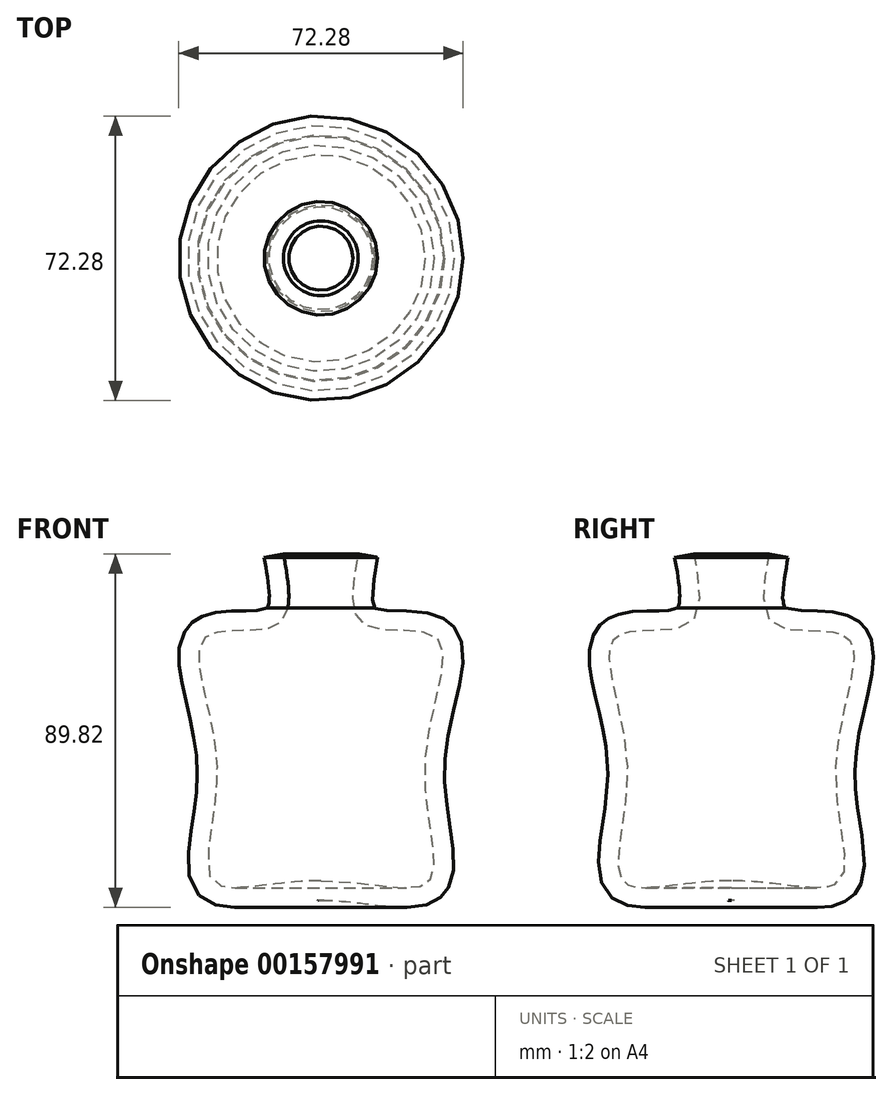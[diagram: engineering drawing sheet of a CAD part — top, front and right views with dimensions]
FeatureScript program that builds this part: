
annotation { "Feature Type Name" : "Feature", "Feature Type Description" : "" }
export const myFeature = defineFeature(function(context is Context, id is Id, definition is map)
    precondition{}
    {
        {
            var Q0;
            Q0=qCreatedBy(makeId("Front.planeOp"),FACE);
            var sketch = newSketch(context, id + "F0", { "sketchPlane" : qUnion([Q0])});
            skFitSpline(sketch, "E0", {"points": [v(0, 0) * mm, v(27.57, 0) * mm, v(26.48, 29.93) * mm, v(29.5, 61.75) * mm, v(11.1, 64.97) * mm, v(9.5, 83.03) * mm], "startDerivative": vector(183.77, -0.53) * mm, "endDerivative": vector(24.04, 135.45) * mm});
            skFitSpline(sketch, "E1.0", {"points": [v(-0.01, -5) * mm, v(1.75, -5) * mm, v(5.27, -5.17) * mm, v(10.39, -5.7) * mm, v(14.42, -6.21) * mm, v(17.49, -6.54) * mm, v(19.7, -6.72) * mm, v(21.87, -6.8) * mm, v(24, -6.7) * mm, v(25.78, -6.43) * mm, v(27.24, -6.01) * mm, v(28.35, -5.57) * mm, v(29.46, -4.96) * mm, v(30.34, -4.3) * mm, v(31, -3.67) * mm, v(31.46, -3.15) * mm, v(31.87, -2.6) * mm, v(32.35, -1.86) * mm, v(32.83, -0.9) * mm, v(33.37, 0.61) * mm, v(33.7, 2.46) * mm, v(33.8, 4.6) * mm, v(33.7, 6.75) * mm, v(33.5, 8.94) * mm, v(33.2, 11.2) * mm, v(32.84, 13.52) * mm, v(32.47, 15.9) * mm, v(32.12, 18.36) * mm, v(31.81, 20.85) * mm, v(31.57, 23.38) * mm, v(31.43, 25.9) * mm, v(31.4, 28.43) * mm, v(31.53, 30.92) * mm, v(31.81, 33.48) * mm, v(32.22, 36.09) * mm, v(32.72, 38.7) * mm, v(33.48, 42.2) * mm, v(34.3, 45.62) * mm, v(35.03, 48.93) * mm, v(35.52, 51.35) * mm, v(35.9, 53.71) * mm, v(36.11, 56.04) * mm, v(36.1, 58.37) * mm, v(35.8, 60.37) * mm, v(35.27, 62.02) * mm, v(34.68, 63.25) * mm, v(34, 64.24) * mm, v(33.37, 64.98) * mm, v(32.83, 65.5) * mm, v(32.26, 65.96) * mm, v(31.5, 66.5) * mm, v(30.51, 67.03) * mm, v(29.35, 67.5) * mm, v(27.84, 67.94) * mm, v(26.01, 68.27) * mm, v(23.88, 68.46) * mm, v(21.8, 68.54) * mm, v(19.81, 68.57) * mm, v(17.95, 68.62) * mm, v(16.3, 68.7) * mm, v(15.16, 68.85) * mm, v(14.46, 69) * mm, v(14.05, 69.1) * mm, v(13.83, 69.19) * mm, v(13.72, 69.24) * mm, v(13.68, 69.26) * mm, v(13.67, 69.27) * mm, v(13.66, 69.27) * mm, v(13.66, 69.27) * mm, v(13.65, 69.28) * mm, v(13.61, 69.34) * mm, v(13.54, 69.46) * mm, v(13.43, 69.74) * mm, v(13.27, 70.33) * mm, v(13.15, 71.4) * mm, v(13.14, 72.75) * mm, v(13.26, 74.87) * mm, v(13.68, 77.98) * mm, v(14.17, 80.75) * mm, v(14.42, 82.16) * mm]});
            skLineSegment(sketch, "E2", {"start": v(9.5, 83.03) * mm, "end": v(14.42, 82.16) * mm});
            skLineSegment(sketch, "E3", {"start": v(0, 0) * mm, "end": v(0, -5) * mm});
            skSolve(sketch);
        }
        {
            var Q0;
            Q0=makeQuery(id+"F0.imprint","IMPRINT",FACE,{"disambiguationData":[TD([[makeQuery(id+"F0.imprint","IMPRINT",EDGE,{"derivedFrom":sQuery(id+"F0.wireOp",EDGE,"E0")}),-1.0]])]});
            var Q1;
            Q1=sQuery(id+"F0.wireOp",EDGE,"E3");
            revolve(context, id + "F1", {"entities" : qUnion([Q0]), "axis" : qUnion([Q1]), "revolveType" : RevolveType.FULL});
        }
        {
            var Q0;
            Q0=qCreatedBy(makeId("Right.planeOp"),FACE);
            var sketch = newSketch(context, id + "F2", { "sketchPlane" : qUnion([Q0])});
            skFitSpline(sketch, "E4", {"points": [v(-32.27, 56.49) * mm, v(-49.92, 56.02) * mm, v(-40.53, 32.25) * mm, v(-29.8, 31.98) * mm], "startDerivative": vector(-63.25, 47.52) * mm, "endDerivative": vector(43.98, 18.52) * mm});
            skSolve(sketch);
        }
        {
            var Q0;
            Q0=sQuery(id+"F2.wireOp",VERTEX,"E4.0.internal");
            var Q1;
            Q1=sQuery(id+"F2.wireOp",EDGE,"E4");
            cPlane(context, id + "F3", {"entities" : qUnion([Q0, Q1]), "cplaneType" : CPlaneType.CURVE_POINT, "offset" : 25 * mm, "width" : 150 * mm, "height" : 150 * mm});
        }
    });
